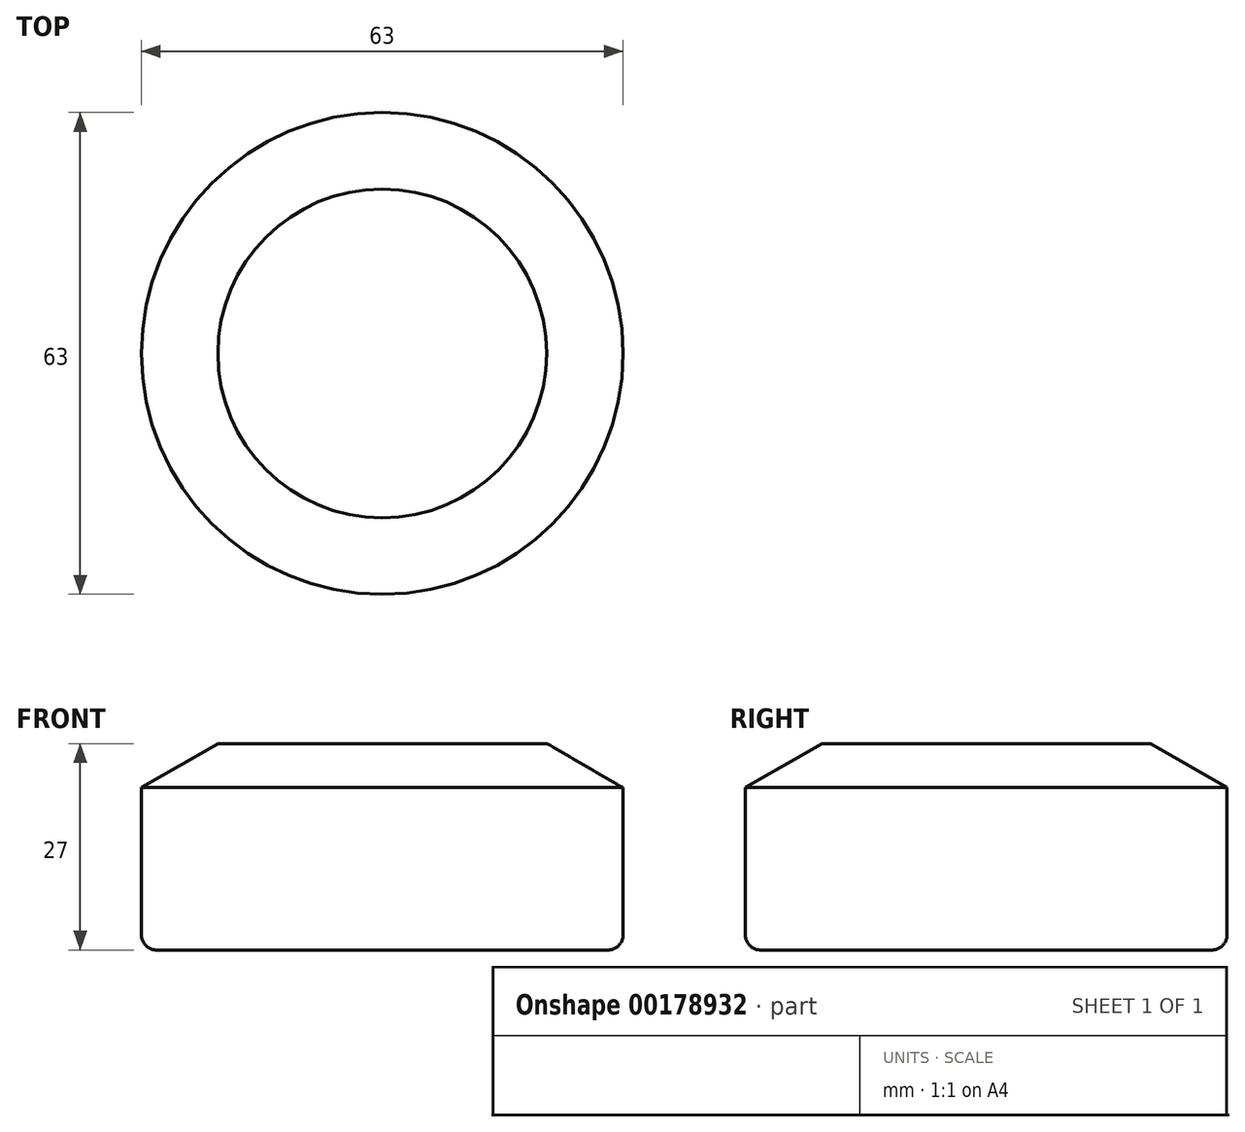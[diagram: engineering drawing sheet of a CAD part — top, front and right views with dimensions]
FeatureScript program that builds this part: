
annotation { "Feature Type Name" : "Feature", "Feature Type Description" : "" }
export const myFeature = defineFeature(function(context is Context, id is Id, definition is map)
    precondition{}
    {
        {
            var Q0;
            Q0=qCreatedBy(makeId("Top.planeOp"),FACE);
            var sketch = newSketch(context, id + "F0", { "sketchPlane" : qUnion([Q0])});
            skCircle(sketch, "E0", {"center": v(0, 0) * mm, "radius": 31.5 * mm});
            skSolve(sketch);
        }
        {
            var Q0;
            Q0 = qSketchRegion(id + "F0", true);
            extrude(context, id + "F1", {"entities" : qUnion([Q0]), "depth" : 27 * mm});
        }
        {
            var Q0;
            Q0=makeQuery(id+"F1.opExtrude","CAP_EDGE",EDGE,{"disambiguationData":[OSD([sQuery(id+"F0.wireOp",EDGE,"E0")])],"isStart":false});
            chamfer(context, id + "F2", {"entities" : qUnion([Q0]), "chamferType" : ChamferType.OFFSET_ANGLE, "width" : 10 * mm, "oppositeDirection" : false, "angle" : 30 * degree, "tangentPropagation" : true});
        }
        {
            var Q0;
            Q0=makeQuery(id+"F1.opExtrude","CAP_EDGE",EDGE,{"disambiguationData":[OSD([sQuery(id+"F0.wireOp",EDGE,"E0")])],"isStart":true});
            fillet(context, id + "F3", {"entities" : qUnion([Q0]), "radius" : 2 * mm, "tangentPropagation" : true, "allowEdgeOverflow" : false});
        }
    });
